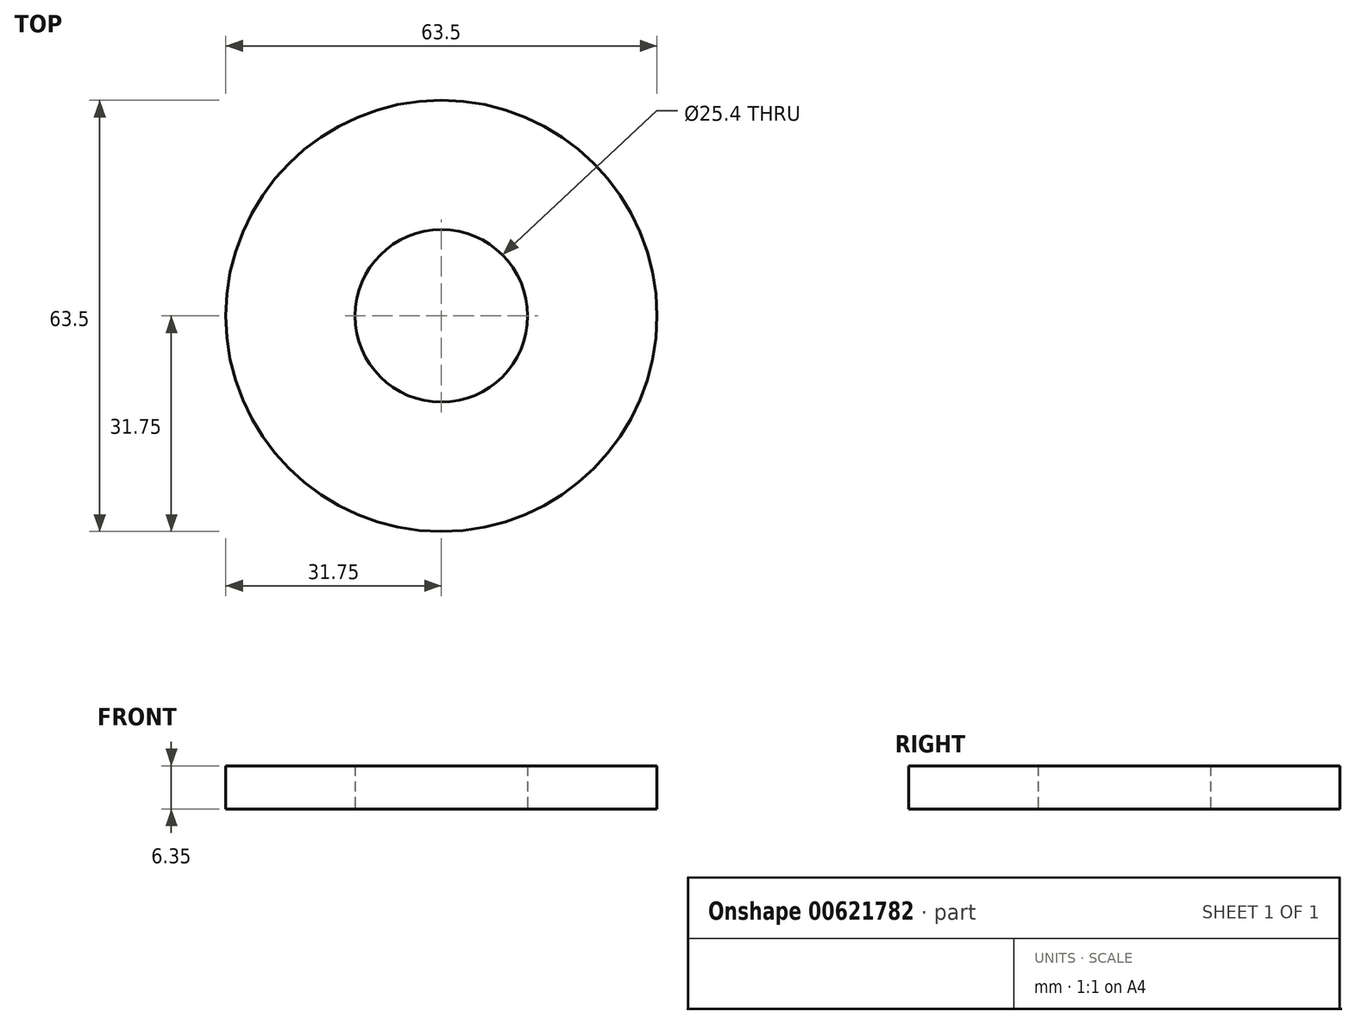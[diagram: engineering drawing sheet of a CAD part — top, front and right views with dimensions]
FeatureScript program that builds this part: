
annotation { "Feature Type Name" : "Feature", "Feature Type Description" : "" }
export const myFeature = defineFeature(function(context is Context, id is Id, definition is map)
    precondition{}
    {
        {
            var Q0;
            Q0=qCreatedBy(makeId("Top.planeOp"),FACE);
            var sketch = newSketch(context, id + "F0", { "sketchPlane" : qUnion([Q0])});
            skCircle(sketch, "E0", {"center": v(0, 0) * mm, "radius": 31.75 * mm});
            skCircle(sketch, "E1", {"center": v(0, 0) * mm, "radius": 12.7 * mm});
            skSolve(sketch);
        }
        {
            var Q0;
            Q0 = qSketchRegion(id + "F0", true);
            extrude(context, id + "F1", {"entities" : qUnion([Q0]), "depth" : 6.35 * mm, "offsetDistance" : 25.4 * mm});
        }
    });
